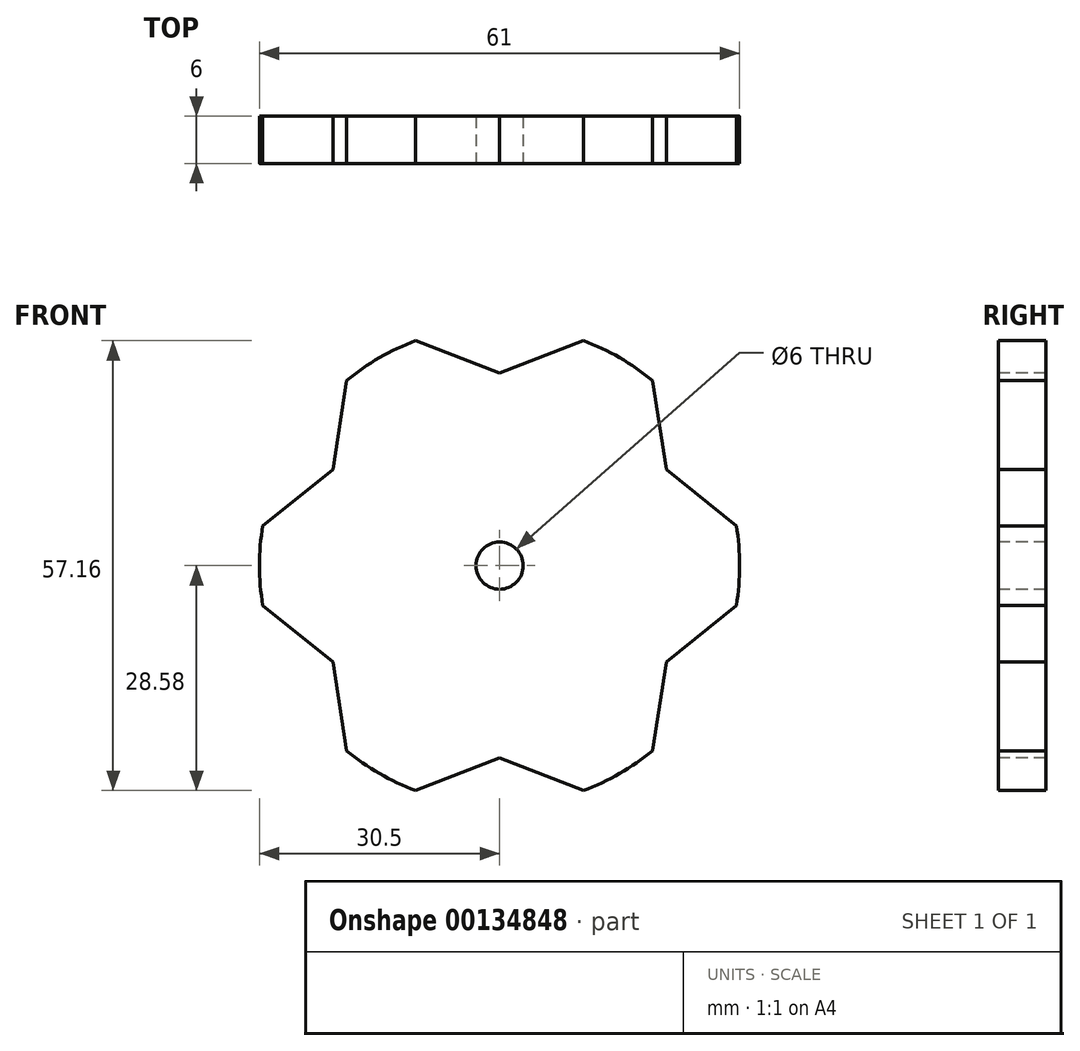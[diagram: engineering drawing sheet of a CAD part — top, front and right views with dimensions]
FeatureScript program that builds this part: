
annotation { "Feature Type Name" : "Feature", "Feature Type Description" : "" }
export const myFeature = defineFeature(function(context is Context, id is Id, definition is map)
    precondition{}
    {
        {
            var Q0;
            Q0=qCreatedBy(makeId("Front.planeOp"),FACE);
            var sketch = newSketch(context, id + "F0", { "sketchPlane" : qUnion([Q0])});
            skCircle(sketch, "E0", {"center": v(0, 0) * mm, "radius": 30.5 * mm});
            skSolve(sketch);
        }
        {
            var Q0;
            Q0=qSketchRegion(id+"F0",true);
            extrude(context, id + "F1", {"entities" : qUnion([Q0]), "depth" : 6 * mm});
        }
        {
            var Q0;
            Q0=makeQuery(id+"F1.opExtrude","CAP_FACE",FACE,{"disambiguationData":[OSD([sQuery(id+"F0.wireOp",EDGE,"E0")])],"isStart":false});
            var sketch = newSketch(context, id + "F2", { "sketchPlane" : qUnion([Q0])});
            skLineSegment(sketch, "E1", {"start": v(0, 45.85) * mm, "end": v(0, 24.45) * mm});
            skLineSegment(sketch, "E2", {"start": v(0, 24.45) * mm, "end": v(29.95, 36.07) * mm});
            skLineSegment(sketch, "E3", {"start": v(29.95, 36.07) * mm, "end": v(0, 45.85) * mm});
            skLineSegment(sketch, "E4.MirrorCS", {"start": v(-29.95, 36.07) * mm, "end": v(0, 45.85) * mm});
            skLineSegment(sketch, "E5.MirrorCS", {"start": v(0, 24.45) * mm, "end": v(-29.95, 36.07) * mm});
            skLineSegment(sketch, "E6.1.0", {"start": v(-21.18, 12.23) * mm, "end": v(-16.26, 43.97) * mm});
            skLineSegment(sketch, "E6.1.1", {"start": v(-21.18, 12.23) * mm, "end": v(-46.2, -7.9) * mm});
            skLineSegment(sketch, "E6.2.0", {"start": v(-21.18, -12.23) * mm, "end": v(-46.2, 7.9) * mm});
            skLineSegment(sketch, "E6.2.1", {"start": v(-21.18, -12.23) * mm, "end": v(-16.26, -43.97) * mm});
            skLineSegment(sketch, "E6.3.0", {"start": v(0, -24.45) * mm, "end": v(-29.95, -36.07) * mm});
            skLineSegment(sketch, "E6.3.1", {"start": v(0, -24.45) * mm, "end": v(29.95, -36.07) * mm});
            skLineSegment(sketch, "E6.4.0", {"start": v(21.18, -12.23) * mm, "end": v(16.26, -43.97) * mm});
            skLineSegment(sketch, "E6.4.1", {"start": v(21.18, -12.23) * mm, "end": v(46.2, 7.9) * mm});
            skLineSegment(sketch, "E6.5.0", {"start": v(21.18, 12.23) * mm, "end": v(46.2, -7.9) * mm});
            skLineSegment(sketch, "E6.5.1", {"start": v(21.18, 12.23) * mm, "end": v(16.26, 43.97) * mm});
            skPoint(sketch, "E6.center", {"position": v(0, 0) * mm});
            skSolve(sketch);
        }
        {
            var Q0;
            {var subQ1=sQuery(id+"F2.wireOp",EDGE,"E6.1.1");var subQ3=sQuery(id+"F2.wireOp",EDGE,"E6.1.0");var subQ5=makeQuery(id+"F2.imprint","INTERSECT",VERTEX,{"derivedFrom":[subQ3,subQ1]});Q0=makeQuery(id+"F2.imprint","IMPRINT",FACE,{"disambiguationData":[TD([[makeQuery(id+"F2.imprint","IMPRINT",EDGE,{"disambiguationData":[TD([[subQ5,-1.0]])],"derivedFrom":subQ3}),1.0]])]});}
            var Q1;
            {var subQ1=sQuery(id+"F2.wireOp",EDGE,"E6.2.1");var subQ3=sQuery(id+"F2.wireOp",EDGE,"E6.2.0");var subQ5=makeQuery(id+"F2.imprint","INTERSECT",VERTEX,{"derivedFrom":[subQ3,subQ1]});Q1=makeQuery(id+"F2.imprint","IMPRINT",FACE,{"disambiguationData":[TD([[makeQuery(id+"F2.imprint","IMPRINT",EDGE,{"disambiguationData":[TD([[subQ5,-1.0]])],"derivedFrom":subQ3}),1.0]])]});}
            var Q2;
            {var subQ1=sQuery(id+"F2.wireOp",EDGE,"E6.3.1");var subQ3=sQuery(id+"F2.wireOp",EDGE,"E6.3.0");var subQ5=makeQuery(id+"F2.imprint","INTERSECT",VERTEX,{"derivedFrom":[subQ3,subQ1]});Q2=makeQuery(id+"F2.imprint","IMPRINT",FACE,{"disambiguationData":[TD([[makeQuery(id+"F2.imprint","IMPRINT",EDGE,{"disambiguationData":[TD([[subQ5,-1.0]])],"derivedFrom":subQ3}),1.0]])]});}
            var Q3;
            {var subQ1=sQuery(id+"F2.wireOp",EDGE,"E6.4.1");var subQ3=sQuery(id+"F2.wireOp",EDGE,"E6.4.0");var subQ5=makeQuery(id+"F2.imprint","INTERSECT",VERTEX,{"derivedFrom":[subQ3,subQ1]});Q3=makeQuery(id+"F2.imprint","IMPRINT",FACE,{"disambiguationData":[TD([[makeQuery(id+"F2.imprint","IMPRINT",EDGE,{"disambiguationData":[TD([[subQ5,-1.0]])],"derivedFrom":subQ3}),1.0]])]});}
            var Q4;
            {var subQ1=sQuery(id+"F2.wireOp",EDGE,"E6.5.1");var subQ3=sQuery(id+"F2.wireOp",EDGE,"E6.5.0");var subQ5=makeQuery(id+"F2.imprint","INTERSECT",VERTEX,{"derivedFrom":[subQ3,subQ1]});Q4=makeQuery(id+"F2.imprint","IMPRINT",FACE,{"disambiguationData":[TD([[makeQuery(id+"F2.imprint","IMPRINT",EDGE,{"disambiguationData":[TD([[subQ5,-1.0]])],"derivedFrom":subQ3}),1.0]])]});}
            var Q5;
            {var subQ0=makeQuery(id+"F1.opExtrude","CAP_EDGE",EDGE,{"disambiguationData":[OSD([sQuery(id+"F0.wireOp",EDGE,"E0")])],"isStart":false});var subQ3=sQuery(id+"F2.wireOp",EDGE,"E1");var subQ4=makeQuery(id+"F2.imprint","INTERSECT",VERTEX,{"derivedFrom":[subQ0,subQ3]});Q5=makeQuery(id+"F2.imprint","IMPRINT",FACE,{"disambiguationData":[TD([[makeQuery(id+"F2.imprint","IMPRINT",EDGE,{"disambiguationData":[TD([[subQ4,1.0]])],"derivedFrom":subQ0}),1.0]])]});}
            var Q6;
            {var subQ0=makeQuery(id+"F1.opExtrude","CAP_EDGE",EDGE,{"disambiguationData":[OSD([sQuery(id+"F0.wireOp",EDGE,"E0")])],"isStart":false});var subQ3=sQuery(id+"F2.wireOp",EDGE,"E1");var subQ4=makeQuery(id+"F2.imprint","INTERSECT",VERTEX,{"derivedFrom":[subQ0,subQ3]});Q6=makeQuery(id+"F2.imprint","IMPRINT",FACE,{"disambiguationData":[TD([[makeQuery(id+"F2.imprint","IMPRINT",EDGE,{"disambiguationData":[TD([[subQ4,-1.0]])],"derivedFrom":subQ0}),1.0]])]});}
            extrude(context, id + "F3", {"entities" : qUnion([Q0, Q1, Q2, Q3, Q4, Q5, Q6]), "operationType" : NewBodyOperationType.REMOVE, "endBound" : BoundingType.THROUGH_ALL, "oppositeDirection" : true, "depth" : 25 * mm});
        }
        {
            var Q0;
            Q0=makeQuery(id+"F1.opExtrude","CAP_FACE",FACE,{"disambiguationData":[OSD([sQuery(id+"F0.wireOp",EDGE,"E0")])],"isStart":false});
            var sketch = newSketch(context, id + "F4", { "sketchPlane" : qUnion([Q0])});
            skCircle(sketch, "E7", {"center": v(0, 0) * mm, "radius": 3 * mm});
            skSolve(sketch);
        }
        {
            var Q0;
            Q0=qSketchRegion(id+"F4",true);
            extrude(context, id + "F5", {"entities" : qUnion([Q0]), "operationType" : NewBodyOperationType.REMOVE, "endBound" : BoundingType.THROUGH_ALL, "oppositeDirection" : true, "depth" : 25 * mm});
        }
    });
